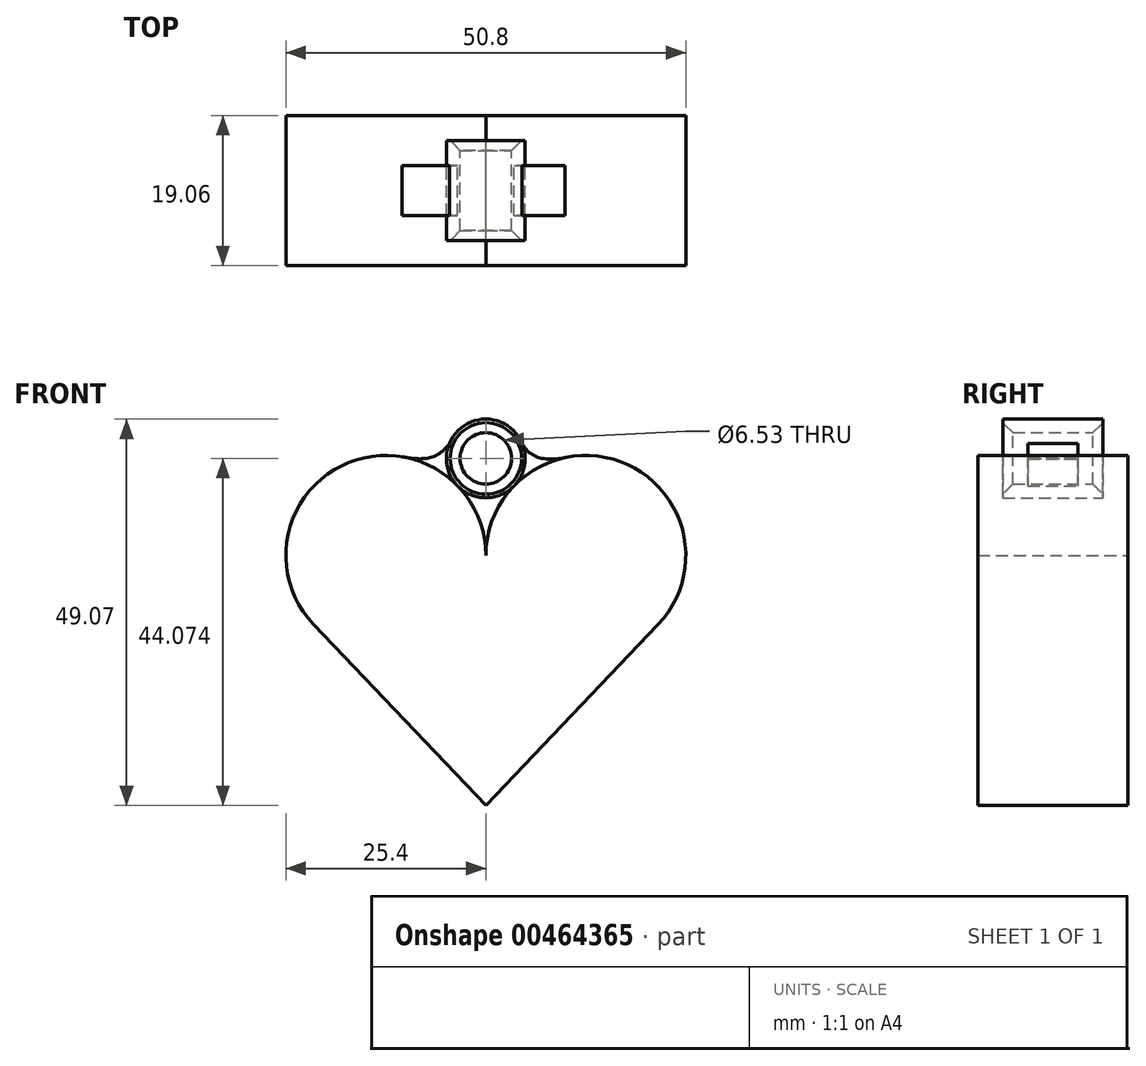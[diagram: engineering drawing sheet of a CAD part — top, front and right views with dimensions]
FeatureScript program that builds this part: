
annotation { "Feature Type Name" : "Feature", "Feature Type Description" : "" }
export const myFeature = defineFeature(function(context is Context, id is Id, definition is map)
    precondition{}
    {
        {
            var Q0;
            Q0=qCreatedBy(makeId("Front.planeOp"),FACE);
            var sketch = newSketch(context, id + "F0", { "sketchPlane" : qUnion([Q0])});
            skCircle(sketch, "E0", {"center": v(-12.7, 12.66) * mm, "radius": 12.7 * mm});
            skCircle(sketch, "E1", {"center": v(12.7, 12.66) * mm, "radius": 12.7 * mm});
            skLineSegment(sketch, "E2", {"start": v(-21.9, 3.9) * mm, "end": v(0, -19.1) * mm});
            skLineSegment(sketch, "E3", {"start": v(0, -19.1) * mm, "end": v(21.9, 3.9) * mm});
            skCircle(sketch, "E4", {"center": v(0, 24.98) * mm, "radius": 5 * mm});
            skCircle(sketch, "E5", {"center": v(0, 24.98) * mm, "radius": 3.26 * mm});
            skFitSpline(sketch, "E6", {"points": [v(-10.62, 25.19) * mm, v(-4.62, 26.9) * mm], "startDerivative": vector(8.34, -1.38) * mm, "endDerivative": vector(4.83, 6.51) * mm});
            skFitSpline(sketch, "E7", {"points": [v(10.11, 25.09) * mm, v(4.62, 26.9) * mm], "startDerivative": vector(-5.6, -1.21) * mm, "endDerivative": vector(-3.25, 6.63) * mm});
            skSolve(sketch);
        }
        {
            var Q0;
            {var subQ0=sQuery(id+"F0.wireOp",EDGE,"E1");var subQ1=makeQuery(id+"F0.imprint","INTERSECT",VERTEX,{"derivedFrom":[subQ0,sQuery(id+"F0.wireOp",EDGE,"E3")]});Q0=makeQuery(id+"F0.imprint","IMPRINT",FACE,{"disambiguationData":[TD([[makeQuery(id+"F0.imprint","IMPRINT",EDGE,{"disambiguationData":[TD([[subQ1,-1.0]])],"derivedFrom":subQ0}),1.0]])]});}
            var Q1;
            {var subQ0=sQuery(id+"F0.wireOp",EDGE,"E0");var subQ1=makeQuery(id+"F0.imprint","INTERSECT",VERTEX,{"derivedFrom":[subQ0,sQuery(id+"F0.wireOp",EDGE,"E4")]});Q1=makeQuery(id+"F0.imprint","IMPRINT",FACE,{"disambiguationData":[TD([[makeQuery(id+"F0.imprint","IMPRINT",EDGE,{"disambiguationData":[TD([[subQ1,1.0]])],"derivedFrom":subQ0}),1.0]])]});}
            var Q2;
            {var subQ0=sQuery(id+"F0.wireOp",EDGE,"E2");Q2=makeQuery(id+"F0.imprint","IMPRINT",FACE,{"disambiguationData":[TD([[makeQuery(id+"F0.imprint","IMPRINT",EDGE,{"derivedFrom":subQ0}),1.0]])]});}
            extrude(context, id + "F1", {"entities" : qUnion([Q0, Q1, Q2]), "endBound" : BoundingType.SYMMETRIC, "depth" : 19.05 * mm});
        }
        {
            var Q0;
            Q0=makeQuery(id+"F0.imprint","IMPRINT",FACE,{"disambiguationData":[TD([[makeQuery(id+"F0.imprint","IMPRINT",EDGE,{"derivedFrom":sQuery(id+"F0.wireOp",EDGE,"E5")}),-1.0]])]});
            extrude(context, id + "F2", {"entities" : qUnion([Q0]), "operationType" : NewBodyOperationType.ADD, "endBound" : BoundingType.SYMMETRIC, "depth" : 12.7 * mm});
        }
        {
            var Q0;
            {var subQ0=sQuery(id+"F0.wireOp",EDGE,"E6");Q0=makeQuery(id+"F0.imprint","IMPRINT",FACE,{"disambiguationData":[TD([[makeQuery(id+"F0.imprint","IMPRINT",EDGE,{"derivedFrom":subQ0}),-1.0]])]});}
            var Q1;
            {var subQ0=sQuery(id+"F0.wireOp",EDGE,"E7");Q1=makeQuery(id+"F0.imprint","IMPRINT",FACE,{"disambiguationData":[TD([[makeQuery(id+"F0.imprint","IMPRINT",EDGE,{"derivedFrom":subQ0}),1.0]])]});}
            extrude(context, id + "F3", {"entities" : qUnion([Q0, Q1]), "endBound" : BoundingType.SYMMETRIC, "depth" : 6.35 * mm});
        }
        {
            var Q0;
            Q0=makeQuery(id+"F2.opExtrude","CAP_EDGE",EDGE,{"disambiguationData":[OSD([sQuery(id+"F0.wireOp",EDGE,"E5")])],"isStart":false});
            var Q1;
            Q1=makeQuery(id+"F2.opExtrude","CAP_EDGE",EDGE,{"disambiguationData":[OSD([sQuery(id+"F0.wireOp",EDGE,"E5")])],"isStart":true});
            chamfer(context, id + "F4", {"entities" : qUnion([Q0, Q1]), "width" : 1.27 * mm, "tangentPropagation" : true});
        }
    });
